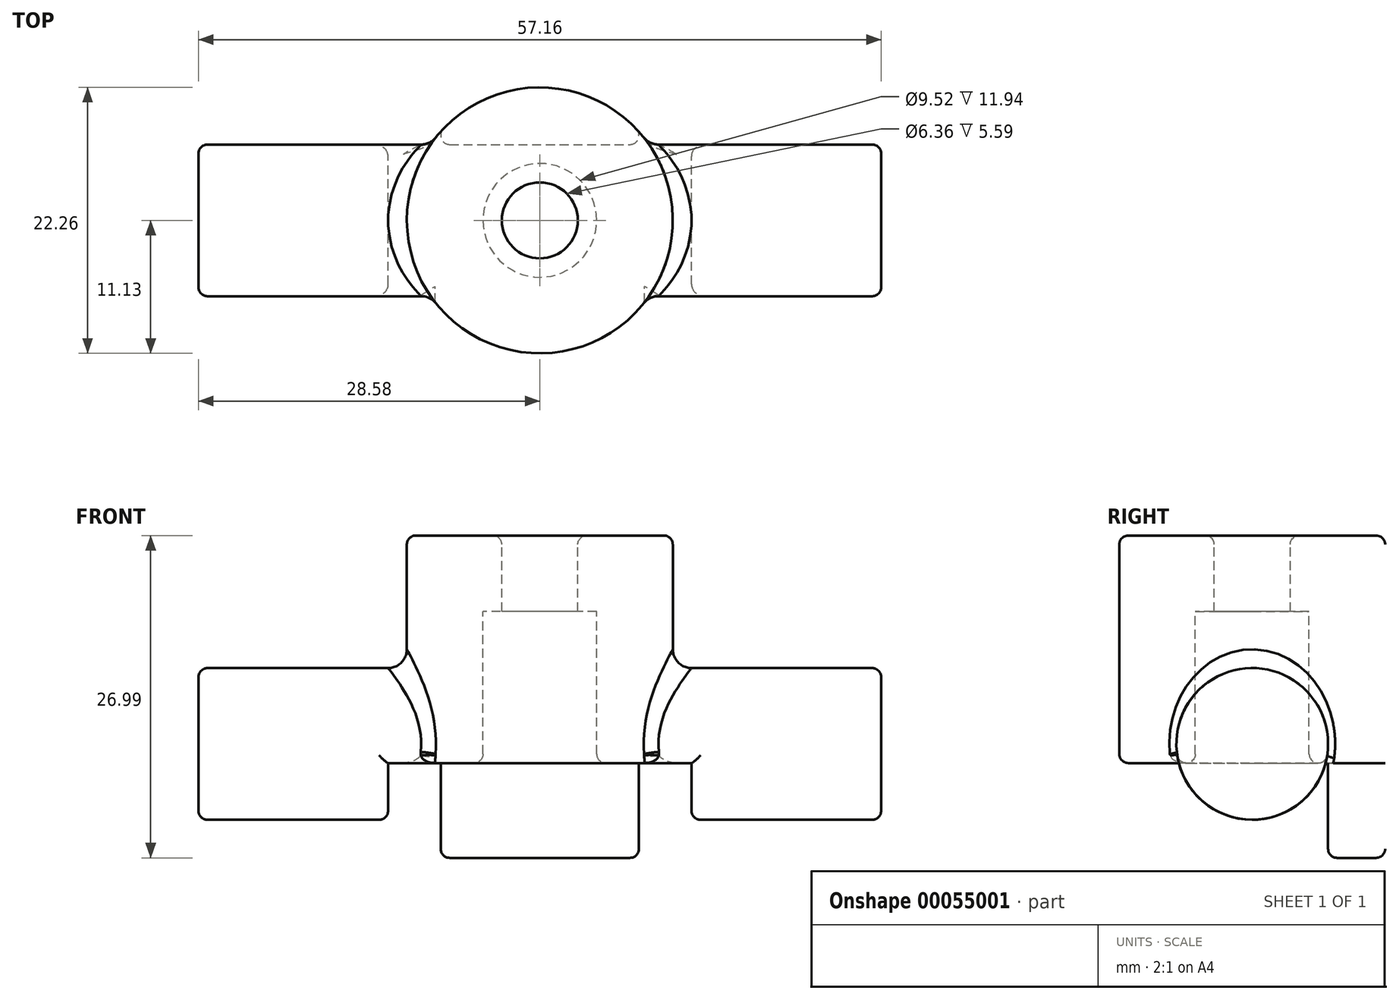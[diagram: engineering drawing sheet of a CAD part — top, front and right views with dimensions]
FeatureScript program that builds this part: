
annotation { "Feature Type Name" : "Feature", "Feature Type Description" : "" }
export const myFeature = defineFeature(function(context is Context, id is Id, definition is map)
    precondition{}
    {
        {
            var Q0;
            Q0=qCreatedBy(makeId("Right.planeOp"),FACE);
            var sketch = newSketch(context, id + "F0", { "sketchPlane" : qUnion([Q0])});
            skLineSegment(sketch, "E0", {"start": v(0, 27.2) * mm, "end": v(0, -27.5) * mm, "construction": true});
            skCircle(sketch, "E1", {"center": v(0, 4.78) * mm, "radius": 6.35 * mm});
            skLineSegment(sketch, "E2", {"start": v(4.76, 0) * mm, "end": v(11.13, 0) * mm});
            skLineSegment(sketch, "E3", {"start": v(11.13, 0) * mm, "end": v(11.13, 22.23) * mm});
            skLineSegment(sketch, "E4", {"start": v(11.13, 22.23) * mm, "end": v(3.17, 22.23) * mm});
            skLineSegment(sketch, "E5", {"start": v(3.18, 22.23) * mm, "end": v(3.18, 15.88) * mm});
            skLineSegment(sketch, "E6", {"start": v(3.17, 15.88) * mm, "end": v(4.76, 15.88) * mm});
            skLineSegment(sketch, "E7", {"start": v(4.76, 15.88) * mm, "end": v(4.76, 0) * mm});
            skSolve(sketch);
        }
        {
            var Q0;
            {var subQ0=sQuery(id+"F0.wireOp",EDGE,"E7");var subQ1=sQuery(id+"F0.wireOp",EDGE,"E1");var subQ2=makeQuery(id+"F0.imprint","INTERSECT",VERTEX,{"disambiguationData":[OD(0.0)],"derivedFrom":[subQ1,subQ0]});Q0=makeQuery(id+"F0.imprint","IMPRINT",FACE,{"disambiguationData":[TD([[makeQuery(id+"F0.imprint","IMPRINT",EDGE,{"disambiguationData":[TD([[subQ2,-1.0]])],"derivedFrom":subQ1}),1.0]])]});}
            var Q1;
            {var subQ0=sQuery(id+"F0.wireOp",EDGE,"E7");var subQ1=sQuery(id+"F0.wireOp",EDGE,"E1");var subQ2=makeQuery(id+"F0.imprint","INTERSECT",VERTEX,{"disambiguationData":[OD(0.0)],"derivedFrom":[subQ1,subQ0]});Q1=makeQuery(id+"F0.imprint","IMPRINT",FACE,{"disambiguationData":[TD([[makeQuery(id+"F0.imprint","IMPRINT",EDGE,{"disambiguationData":[TD([[subQ2,1.0]])],"derivedFrom":subQ1}),1.0]])]});}
            extrude(context, id + "F1", {"entities" : qUnion([Q0, Q1]), "endBound" : BoundingType.SYMMETRIC, "depth" : 57.15 * mm});
        }
        {
            var Q0;
            {var subQ0=sQuery(id+"F0.wireOp",EDGE,"E7");var subQ1=sQuery(id+"F0.wireOp",EDGE,"E1");var subQ2=makeQuery(id+"F0.imprint","INTERSECT",VERTEX,{"disambiguationData":[OD(0.0)],"derivedFrom":[subQ1,subQ0]});Q0=makeQuery(id+"F0.imprint","IMPRINT",FACE,{"disambiguationData":[TD([[makeQuery(id+"F0.imprint","IMPRINT",EDGE,{"disambiguationData":[TD([[subQ2,1.0]])],"derivedFrom":subQ1}),1.0]])]});}
            var Q1;
            {var subQ0=sQuery(id+"F0.wireOp",EDGE,"E2");Q1=makeQuery(id+"F0.imprint","IMPRINT",FACE,{"disambiguationData":[TD([[makeQuery(id+"F0.imprint","IMPRINT",EDGE,{"derivedFrom":subQ0}),1.0]])]});}
            var Q2;
            Q2=sQuery(id+"F0.wireOp",EDGE,"E0");
            revolve(context, id + "F2", {"entities" : qUnion([Q0, Q1]), "axis" : qUnion([Q2]), "revolveType" : RevolveType.FULL});
        }
        {
            var Q0;
            Q0=makeQuery(id+"F1.opExtrude","SWEPT_BODY",BODY,{"disambiguationData":[OSD([sQuery(id+"F0.wireOp",EDGE,"E1")])]});
            var Q1;
            Q1=makeQuery(id+"F2.opRevolve","SWEPT_BODY",BODY,{"disambiguationData":[OSD([sQuery(id+"F0.wireOp",EDGE,"E2"),sQuery(id+"F0.wireOp",EDGE,"E3"),sQuery(id+"F0.wireOp",EDGE,"E4"),sQuery(id+"F0.wireOp",EDGE,"E5"),sQuery(id+"F0.wireOp",EDGE,"E6"),sQuery(id+"F0.wireOp",EDGE,"E7")])]});
            booleanBodies(context, id + "F3", {"operationType" : BooleanOperationType.UNION, "tools" : qUnion([Q0, Q1])});
        }
        {
            var Q0;
            Q0=qCreatedBy(makeId("Front.planeOp"),FACE);
            var sketch = newSketch(context, id + "F4", { "sketchPlane" : qUnion([Q0])});
            skLineSegment(sketch, "E8", {"start": v(12.7, -1.57) * mm, "end": v(0, -1.57) * mm});
            skLineSegment(sketch, "E9", {"start": v(0, 3.18) * mm, "end": v(12.7, 3.18) * mm});
            skLineSegment(sketch, "E10", {"start": v(12.7, 3.18) * mm, "end": v(12.7, -1.57) * mm});
            skLineSegment(sketch, "E11.MirrorCS", {"start": v(0, 3.18) * mm, "end": v(-12.7, 3.18) * mm});
            skLineSegment(sketch, "E12.MirrorCS", {"start": v(-12.7, 3.18) * mm, "end": v(-12.7, -1.57) * mm});
            skLineSegment(sketch, "E13.MirrorCS", {"start": v(-12.7, -1.57) * mm, "end": v(0, -1.57) * mm});
            skSolve(sketch);
        }
        {
            var Q0;
            Q0=qSketchRegion(id+"F4",true);
            extrude(context, id + "F5", {"entities" : qUnion([Q0]), "operationType" : NewBodyOperationType.REMOVE, "endBound" : BoundingType.SYMMETRIC, "depth" : 25.4 * mm});
        }
        {
            var Q0;
            Q0=qCreatedBy(makeId("Top.planeOp"),FACE);
            var sketch = newSketch(context, id + "F6", { "sketchPlane" : qUnion([Q0])});
            skCircle(sketch, "E14", {"center": v(0, 0) * mm, "radius": 4.76 * mm});
            skSolve(sketch);
        }
        {
            var Q0;
            Q0=qSketchRegion(id+"F6",true);
            extrude(context, id + "F7", {"entities" : qUnion([Q0]), "operationType" : NewBodyOperationType.REMOVE, "depth" : 15.88 * mm});
        }
        {
            var Q0;
            Q0=qCreatedBy(makeId("Top.planeOp"),FACE);
            var sketch = newSketch(context, id + "F8", { "sketchPlane" : qUnion([Q0])});
            skArc(sketch, "E15", {"start": v(9.13, 6.35) * mm, "mid": v(0, 11.13) * mm, "end": v(-9.13, 6.35) * mm});
            skLineSegment(sketch, "E16", {"start": v(-9.13, 6.35) * mm, "end": v(9.13, 6.35) * mm});
            skSolve(sketch);
        }
        {
            var Q0;
            Q0=qSketchRegion(id+"F8",true);
            extrude(context, id + "F9", {"entities" : qUnion([Q0]), "operationType" : NewBodyOperationType.ADD, "endBound" : BoundingType.SYMMETRIC, "oppositeDirection" : true, "depth" : 9.52 * mm});
        }
        {
            var Q0;
            Q0=makeQuery(id+"F9.opExtrude","CAP_FACE",FACE,{"disambiguationData":[OSD([sQuery(id+"F8.wireOp",EDGE,"E15"),sQuery(id+"F8.wireOp",EDGE,"E16")])],"isStart":false});
            var Q1;
            Q1=makeQuery(id+"F2.opRevolve","SWEPT_EDGE",EDGE,{"disambiguationData":[OSD([sQuery(id+"F0.wireOp",EDGE,"E3"),sQuery(id+"F0.wireOp",EDGE,"E4")])]});
            var Q2;
            Q2=makeQuery(id+"F1.opExtrude","CAP_FACE",FACE,{"disambiguationData":[OSD([sQuery(id+"F0.wireOp",EDGE,"E1")])],"isStart":true});
            var Q3;
            Q3=makeQuery(id+"F1.opExtrude","CAP_FACE",FACE,{"disambiguationData":[OSD([sQuery(id+"F0.wireOp",EDGE,"E1")])],"isStart":false});
            var Q4;
            {var subQ0=sQuery(id+"F0.wireOp",EDGE,"E1");Q4=makeQuery(id+"F5.boolean.opBoolean","INTERSECT",EDGE,{"disambiguationData":[OD(0.0)],"derivedFrom":[makeQuery(id+"F3.opBoolean","SPLIT",FACE,{"disambiguationData":[TD([makeQuery(id+"F1.opExtrude","CAP_FACE",FACE,{"disambiguationData":[OSD([subQ0])],"isStart":true}),makeQuery(id+"F1.opExtrude","CAP_FACE",FACE,{"disambiguationData":[OSD([subQ0])],"isStart":false}),makeQuery(id+"F2.opRevolve","SWEPT_FACE",FACE,{"disambiguationData":[OSD([sQuery(id+"F0.wireOp",EDGE,"E2")])]}),makeQuery(id+"F2.opRevolve","SWEPT_FACE",FACE,{"disambiguationData":[OSD([sQuery(id+"F0.wireOp",EDGE,"E3")])]}),makeQuery(id+"F2.opRevolve","SWEPT_FACE",FACE,{"disambiguationData":[OSD([sQuery(id+"F0.wireOp",EDGE,"E7")])]})])],"derivedFrom":makeQuery(id+"F1.opExtrude","SWEPT_FACE",FACE,{"disambiguationData":[OSD([subQ0])]})}),makeQuery(id+"F5.opExtrude","SWEPT_FACE",FACE,{"disambiguationData":[OSD([sQuery(id+"F4.wireOp",EDGE,"E9"),sQuery(id+"F4.wireOp",EDGE,"E11.MirrorCS")])]})]});}
            var Q5;
            Q5=makeQuery(id+"F5.boolean.opBoolean","INTERSECT",EDGE,{"disambiguationData":[OD(0.0)],"derivedFrom":[makeQuery(id+"F2.opRevolve","SWEPT_FACE",FACE,{"disambiguationData":[OSD([sQuery(id+"F0.wireOp",EDGE,"E3")])]}),makeQuery(id+"F5.opExtrude","SWEPT_FACE",FACE,{"disambiguationData":[OSD([sQuery(id+"F4.wireOp",EDGE,"E9"),sQuery(id+"F4.wireOp",EDGE,"E11.MirrorCS")])]})]});
            var Q6;
            {var subQ0=sQuery(id+"F0.wireOp",EDGE,"E1");Q6=makeQuery(id+"F5.boolean.opBoolean","INTERSECT",EDGE,{"disambiguationData":[OD(2.0)],"derivedFrom":[makeQuery(id+"F3.opBoolean","SPLIT",FACE,{"disambiguationData":[TD([makeQuery(id+"F1.opExtrude","CAP_FACE",FACE,{"disambiguationData":[OSD([subQ0])],"isStart":true}),makeQuery(id+"F1.opExtrude","CAP_FACE",FACE,{"disambiguationData":[OSD([subQ0])],"isStart":false}),makeQuery(id+"F2.opRevolve","SWEPT_FACE",FACE,{"disambiguationData":[OSD([sQuery(id+"F0.wireOp",EDGE,"E2")])]}),makeQuery(id+"F2.opRevolve","SWEPT_FACE",FACE,{"disambiguationData":[OSD([sQuery(id+"F0.wireOp",EDGE,"E3")])]}),makeQuery(id+"F2.opRevolve","SWEPT_FACE",FACE,{"disambiguationData":[OSD([sQuery(id+"F0.wireOp",EDGE,"E7")])]})])],"derivedFrom":makeQuery(id+"F1.opExtrude","SWEPT_FACE",FACE,{"disambiguationData":[OSD([subQ0])]})}),makeQuery(id+"F5.opExtrude","SWEPT_FACE",FACE,{"disambiguationData":[OSD([sQuery(id+"F4.wireOp",EDGE,"E9"),sQuery(id+"F4.wireOp",EDGE,"E11.MirrorCS")])]})]});}
            var Q7;
            {var subQ0=sQuery(id+"F0.wireOp",EDGE,"E1");Q7=makeQuery(id+"F5.boolean.opBoolean","INTERSECT",EDGE,{"derivedFrom":[makeQuery(id+"F3.opBoolean","SPLIT",FACE,{"disambiguationData":[TD([makeQuery(id+"F1.opExtrude","CAP_FACE",FACE,{"disambiguationData":[OSD([subQ0])],"isStart":true}),makeQuery(id+"F1.opExtrude","CAP_FACE",FACE,{"disambiguationData":[OSD([subQ0])],"isStart":false}),makeQuery(id+"F2.opRevolve","SWEPT_FACE",FACE,{"disambiguationData":[OSD([sQuery(id+"F0.wireOp",EDGE,"E2")])]}),makeQuery(id+"F2.opRevolve","SWEPT_FACE",FACE,{"disambiguationData":[OSD([sQuery(id+"F0.wireOp",EDGE,"E3")])]}),makeQuery(id+"F2.opRevolve","SWEPT_FACE",FACE,{"disambiguationData":[OSD([sQuery(id+"F0.wireOp",EDGE,"E7")])]})])],"derivedFrom":makeQuery(id+"F1.opExtrude","SWEPT_FACE",FACE,{"disambiguationData":[OSD([subQ0])]})}),makeQuery(id+"F5.opExtrude","SWEPT_FACE",FACE,{"disambiguationData":[OSD([sQuery(id+"F4.wireOp",EDGE,"E10")])]})]});}
            var Q8;
            {var subQ0=sQuery(id+"F0.wireOp",EDGE,"E1");Q8=makeQuery(id+"F5.boolean.opBoolean","INTERSECT",EDGE,{"derivedFrom":[makeQuery(id+"F3.opBoolean","SPLIT",FACE,{"disambiguationData":[TD([makeQuery(id+"F1.opExtrude","CAP_FACE",FACE,{"disambiguationData":[OSD([subQ0])],"isStart":true}),makeQuery(id+"F1.opExtrude","CAP_FACE",FACE,{"disambiguationData":[OSD([subQ0])],"isStart":false}),makeQuery(id+"F2.opRevolve","SWEPT_FACE",FACE,{"disambiguationData":[OSD([sQuery(id+"F0.wireOp",EDGE,"E2")])]}),makeQuery(id+"F2.opRevolve","SWEPT_FACE",FACE,{"disambiguationData":[OSD([sQuery(id+"F0.wireOp",EDGE,"E3")])]}),makeQuery(id+"F2.opRevolve","SWEPT_FACE",FACE,{"disambiguationData":[OSD([sQuery(id+"F0.wireOp",EDGE,"E7")])]})])],"derivedFrom":makeQuery(id+"F1.opExtrude","SWEPT_FACE",FACE,{"disambiguationData":[OSD([subQ0])]})}),makeQuery(id+"F5.opExtrude","SWEPT_FACE",FACE,{"disambiguationData":[OSD([sQuery(id+"F4.wireOp",EDGE,"E12.MirrorCS")])]})]});}
            var Q9;
            {var subQ0=sQuery(id+"F0.wireOp",EDGE,"E1");Q9=makeQuery(id+"F5.boolean.opBoolean","INTERSECT",EDGE,{"disambiguationData":[OD(1.0)],"derivedFrom":[makeQuery(id+"F3.opBoolean","SPLIT",FACE,{"disambiguationData":[TD([makeQuery(id+"F1.opExtrude","CAP_FACE",FACE,{"disambiguationData":[OSD([subQ0])],"isStart":true}),makeQuery(id+"F1.opExtrude","CAP_FACE",FACE,{"disambiguationData":[OSD([subQ0])],"isStart":false}),makeQuery(id+"F2.opRevolve","SWEPT_FACE",FACE,{"disambiguationData":[OSD([sQuery(id+"F0.wireOp",EDGE,"E2")])]}),makeQuery(id+"F2.opRevolve","SWEPT_FACE",FACE,{"disambiguationData":[OSD([sQuery(id+"F0.wireOp",EDGE,"E3")])]}),makeQuery(id+"F2.opRevolve","SWEPT_FACE",FACE,{"disambiguationData":[OSD([sQuery(id+"F0.wireOp",EDGE,"E7")])]})])],"derivedFrom":makeQuery(id+"F1.opExtrude","SWEPT_FACE",FACE,{"disambiguationData":[OSD([subQ0])]})}),makeQuery(id+"F5.opExtrude","SWEPT_FACE",FACE,{"disambiguationData":[OSD([sQuery(id+"F4.wireOp",EDGE,"E9"),sQuery(id+"F4.wireOp",EDGE,"E11.MirrorCS")])]})]});}
            var Q10;
            {var subQ0=sQuery(id+"F0.wireOp",EDGE,"E1");Q10=makeQuery(id+"F5.boolean.opBoolean","INTERSECT",EDGE,{"disambiguationData":[OD(3.0)],"derivedFrom":[makeQuery(id+"F3.opBoolean","SPLIT",FACE,{"disambiguationData":[TD([makeQuery(id+"F1.opExtrude","CAP_FACE",FACE,{"disambiguationData":[OSD([subQ0])],"isStart":true}),makeQuery(id+"F1.opExtrude","CAP_FACE",FACE,{"disambiguationData":[OSD([subQ0])],"isStart":false}),makeQuery(id+"F2.opRevolve","SWEPT_FACE",FACE,{"disambiguationData":[OSD([sQuery(id+"F0.wireOp",EDGE,"E2")])]}),makeQuery(id+"F2.opRevolve","SWEPT_FACE",FACE,{"disambiguationData":[OSD([sQuery(id+"F0.wireOp",EDGE,"E3")])]}),makeQuery(id+"F2.opRevolve","SWEPT_FACE",FACE,{"disambiguationData":[OSD([sQuery(id+"F0.wireOp",EDGE,"E7")])]})])],"derivedFrom":makeQuery(id+"F1.opExtrude","SWEPT_FACE",FACE,{"disambiguationData":[OSD([subQ0])]})}),makeQuery(id+"F5.opExtrude","SWEPT_FACE",FACE,{"disambiguationData":[OSD([sQuery(id+"F4.wireOp",EDGE,"E9"),sQuery(id+"F4.wireOp",EDGE,"E11.MirrorCS")])]})]});}
            var Q11;
            {var subQ0=sQuery(id+"F8.wireOp",EDGE,"E16");var subQ1=sQuery(id+"F8.wireOp",EDGE,"E15");Q11=makeQuery(id+"F9.opExtrude","SWEPT_EDGE",EDGE,{"disambiguationData":[OSD([subQ1,subQ0]),TDD([makeQuery(id+"F8.imprint","INTERSECT",VERTEX,{"disambiguationData":[OD(1.0)],"derivedFrom":[subQ1,subQ0]})])]});}
            var Q12;
            {var subQ0=sQuery(id+"F8.wireOp",EDGE,"E16");var subQ1=sQuery(id+"F8.wireOp",EDGE,"E15");Q12=makeQuery(id+"F9.opExtrude","SWEPT_EDGE",EDGE,{"disambiguationData":[OSD([subQ1,subQ0]),TDD([makeQuery(id+"F8.imprint","INTERSECT",VERTEX,{"disambiguationData":[OD(0.0)],"derivedFrom":[subQ1,subQ0]})])]});}
            var Q13;
            Q13=makeQuery(id+"F7.boolean.opBoolean","INTERSECT",EDGE,{"derivedFrom":[makeQuery(id+"F5.boolean.opBoolean","COPY",FACE,{"derivedFrom":makeQuery(id+"F5.opExtrude","SWEPT_FACE",FACE,{"disambiguationData":[OSD([sQuery(id+"F4.wireOp",EDGE,"E9"),sQuery(id+"F4.wireOp",EDGE,"E11.MirrorCS")])]})}),makeQuery(id+"F7.opExtrude","SWEPT_FACE",FACE,{"disambiguationData":[OSD([sQuery(id+"F6.wireOp",EDGE,"E14")])]})]});
            var Q14;
            Q14=makeQuery(id+"F2.opRevolve","SWEPT_EDGE",EDGE,{"disambiguationData":[OSD([sQuery(id+"F0.wireOp",EDGE,"E4"),sQuery(id+"F0.wireOp",EDGE,"E5")])]});
            fillet(context, id + "F10", {"entities" : qUnion([Q0, Q1, Q2, Q3, Q4, Q5, Q6, Q7, Q8, Q9, Q10, Q11, Q12, Q13, Q14]), "radius" : 0.76 * mm, "tangentPropagation" : true, "allowEdgeOverflow" : false});
        }
        {
            var Q0;
            Q0=makeQuery(id+"F3.opBoolean","INTERSECT",EDGE,{"disambiguationData":[OD(1.0)],"derivedFrom":[makeQuery(id+"F1.opExtrude","SWEPT_FACE",FACE,{"disambiguationData":[OSD([sQuery(id+"F0.wireOp",EDGE,"E1")])]}),makeQuery(id+"F2.opRevolve","SWEPT_FACE",FACE,{"disambiguationData":[OSD([sQuery(id+"F0.wireOp",EDGE,"E3")])]})]});
            var Q1;
            Q1=makeQuery(id+"F3.opBoolean","INTERSECT",EDGE,{"disambiguationData":[OD(0.0)],"derivedFrom":[makeQuery(id+"F1.opExtrude","SWEPT_FACE",FACE,{"disambiguationData":[OSD([sQuery(id+"F0.wireOp",EDGE,"E1")])]}),makeQuery(id+"F2.opRevolve","SWEPT_FACE",FACE,{"disambiguationData":[OSD([sQuery(id+"F0.wireOp",EDGE,"E3")])]})]});
            fillet(context, id + "F11", {"entities" : qUnion([Q0, Q1]), "radius" : 1.57 * mm, "tangentPropagation" : true, "allowEdgeOverflow" : false});
        }
    });
